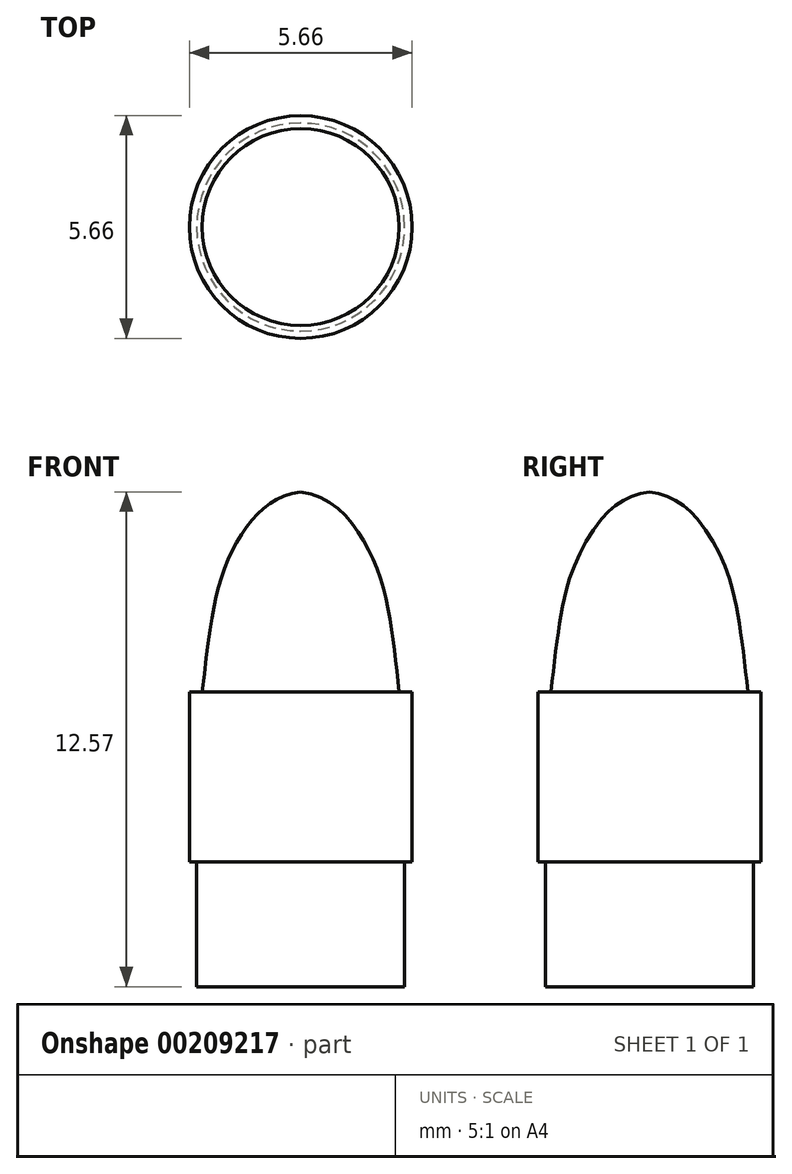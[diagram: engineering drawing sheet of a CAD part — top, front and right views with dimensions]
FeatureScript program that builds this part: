
annotation { "Feature Type Name" : "Feature", "Feature Type Description" : "" }
export const myFeature = defineFeature(function(context is Context, id is Id, definition is map)
    precondition{}
    {
        {
            var Q0;
            Q0=qCreatedBy(makeId("Front.planeOp"),FACE);
            var sketch = newSketch(context, id + "F0", { "sketchPlane" : qUnion([Q0])});
            skLineSegment(sketch, "E0", {"start": v(0, 0) * mm, "end": v(-2.64, 0) * mm});
            skLineSegment(sketch, "E1", {"start": v(-2.83, 7.5) * mm, "end": v(-2.83, 3.18) * mm});
            skLineSegment(sketch, "E2", {"start": v(-2.83, 3.18) * mm, "end": v(-2.64, 3.18) * mm});
            skLineSegment(sketch, "E3", {"start": v(-2.64, 3.18) * mm, "end": v(-2.64, 0) * mm});
            skLineSegment(sketch, "E4", {"start": v(-2.83, 7.5) * mm, "end": v(-2.5, 7.5) * mm});
            skLineSegment(sketch, "E5", {"start": v(0, 0) * mm, "end": v(0, 12.57) * mm});
            skFitSpline(sketch, "E6", {"points": [v(0, 12.57) * mm, v(-1.13, 11.98) * mm, v(-1.96, 10.56) * mm, v(-2.5, 7.5) * mm], "startDerivative": vector(-5.36, -0.85) * mm, "endDerivative": vector(-1.26, -10.96) * mm});
            skSolve(sketch);
        }
        {
            var Q0;
            Q0=makeQuery(id+"F0.imprint","IMPRINT",FACE,{"disambiguationData":[TD([[makeQuery(id+"F0.imprint","IMPRINT",EDGE,{"derivedFrom":sQuery(id+"F0.wireOp",EDGE,"E0")}),-1.0]])]});
            var Q1;
            Q1=sQuery(id+"F0.wireOp",EDGE,"E5");
            revolve(context, id + "F1", {"entities" : qUnion([Q0]), "axis" : qUnion([Q1]), "revolveType" : RevolveType.FULL});
        }
    });
